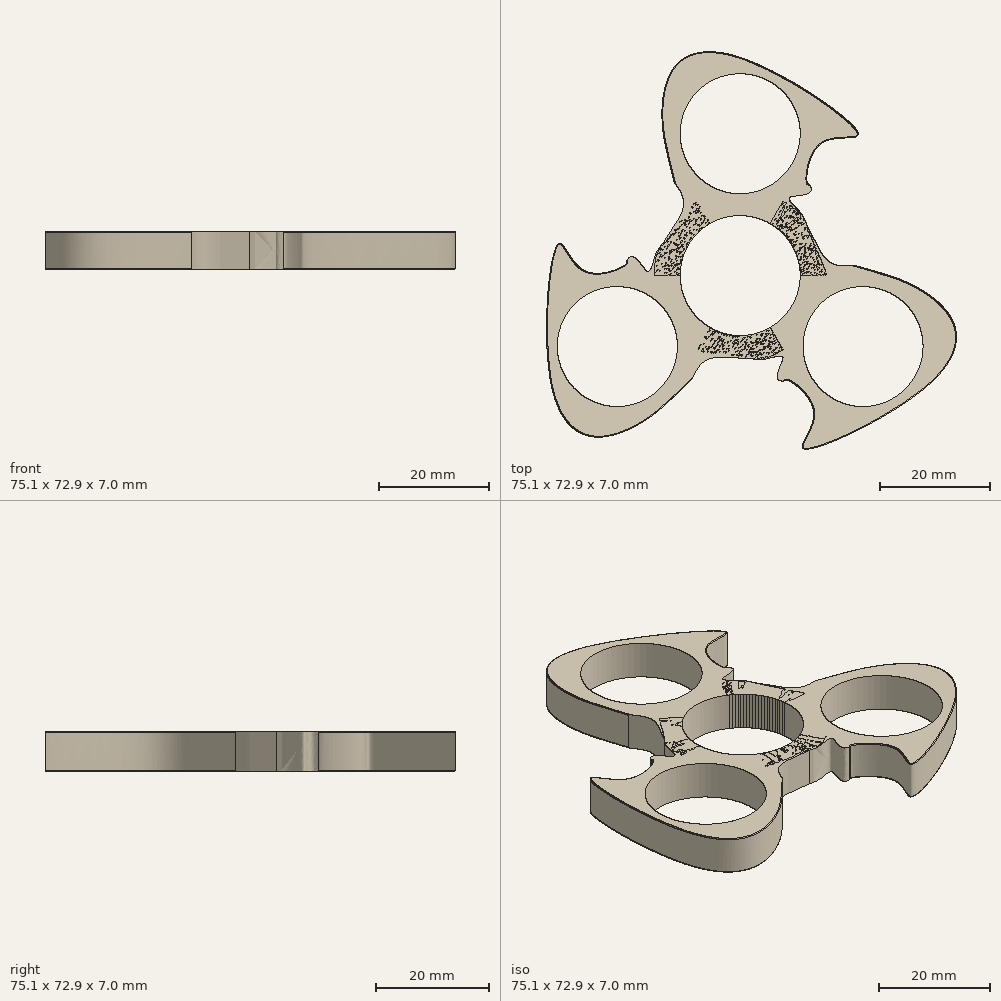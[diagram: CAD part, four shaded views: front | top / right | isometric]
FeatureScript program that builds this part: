
annotation { "Feature Type Name" : "Feature", "Feature Type Description" : "" }
export const myFeature = defineFeature(function(context is Context, id is Id, definition is map)
    precondition{}
    {
        {
            var Q0;
            Q0=qCreatedBy(makeId("Top.planeOp"),FACE);
            var sketch = newSketch(context, id + "F0", { "sketchPlane" : qUnion([Q0])});
            skCircle(sketch, "E0", {"center": v(0, 0) * mm, "radius": 11 * mm});
            skCircle(sketch, "E1", {"center": v(0, 0) * mm, "radius": 40 * mm, "construction": true});
            skCircle(sketch, "E2", {"center": v(0, 26) * mm, "radius": 11 * mm});
            skFitSpline(sketch, "E3", {"points": [v(-12.1, 17.16) * mm, v(-14.27, 27.57) * mm, v(-12.1, 38.13) * mm, v(0, 40) * mm, v(21.66, 25.74) * mm, v(15.06, 24.27) * mm, v(12.3, 17.02) * mm, v(12.7, 16.69) * mm], "startDerivative": vector(-15.95, 69.21) * mm, "endDerivative": vector(13.25, -3.97) * mm});
            skFitSpline(sketch, "E4", {"points": [v(-12.1, 17.16) * mm, v(-10.42, 12.54) * mm, v(-15, 4.47) * mm, v(-15.73, 0) * mm], "startDerivative": vector(10.04, -14.18) * mm, "endDerivative": vector(0.47, -14.35) * mm});
            skFitSpline(sketch, "E5", {"points": [v(12.7, 16.69) * mm, v(9.2, 14.37) * mm, v(10.84, 11.8) * mm, v(12.7, 7.77) * mm, v(15.98, 0) * mm], "startDerivative": vector(19.54, -29.66) * mm, "endDerivative": vector(8.65, -25.53) * mm});
            skLineSegment(sketch, "E6", {"start": v(-15.73, 0) * mm, "end": v(-11, 0) * mm});
            skLineSegment(sketch, "E7", {"start": v(-11, 0) * mm, "end": v(15.98, 0) * mm});
            skFitSpline(sketch, "E8", {"points": [v(12.7, 16.69) * mm, v(12.45, 17.1) * mm, v(12.21, 17.9) * mm, v(12.21, 17.9) * mm], "startDerivative": vector(-0.62, 0.64) * mm, "endDerivative": vector(-0.34, -2.15) * mm});
            skSolve(sketch);
        }
        {
            var Q0;
            Q0=makeQuery(id+"F0.imprint","IMPRINT",FACE,{"disambiguationData":[TD([[makeQuery(id+"F0.imprint","IMPRINT",EDGE,{"derivedFrom":sQuery(id+"F0.wireOp",EDGE,"E2")}),-1.0]])]});
            extrude(context, id + "F1", {"entities" : qUnion([Q0]), "depth" : 7 * mm, "offsetDistance" : 25 * mm});
        }
        {
            var Q0;
            Q0=qCreatedBy(makeId("Front.planeOp"),FACE);
            var sketch = newSketch(context, id + "F2", { "sketchPlane" : qUnion([Q0])});
            skLineSegment(sketch, "E9", {"start": v(0, 47.56) * mm, "end": v(0, -33.84) * mm, "construction": true});
            skSolve(sketch);
        }
        {
            var Q0;
            Q0=makeQuery(id+"F1.opExtrude","SWEPT_FACE",FACE,{"disambiguationData":[OSD([sQuery(id+"F0.wireOp",EDGE,"E3")])]});
            fillet(context, id + "F3", {"entities" : qUnion([Q0]), "radius" : 0.16 * mm, "tangentPropagation" : true, "allowEdgeOverflow" : false});
        }
        {
            var Q0;
            Q0=makeQuery(id+"F1.opExtrude","SWEPT_BODY",BODY,{"disambiguationData":[OSD([sQuery(id+"F0.wireOp",EDGE,"E0"),sQuery(id+"F0.wireOp",EDGE,"E2"),sQuery(id+"F0.wireOp",EDGE,"E3"),sQuery(id+"F0.wireOp",EDGE,"E4"),sQuery(id+"F0.wireOp",EDGE,"E5"),sQuery(id+"F0.wireOp",EDGE,"E6"),sQuery(id+"F0.wireOp",EDGE,"E7"),sQuery(id+"F0.wireOp",EDGE,"E8")])]});
            var Q1;
            Q1=sQuery(id+"F2.wireOp",EDGE,"E9");
            circularPattern(context, id + "F4", {"entities" : qUnion([Q0]), "axis" : qUnion([Q1]), "angle" : 360 * degree, "instanceCount" : 3, "equalSpace" : true});
        }
    });
